# Revit family: ROSENBERG_KHAG-S
name_source: partatom
category: Wyposażenie mechaniczne
revit_build: Autodesk Revit 2017 (Build: 20160225_1515(x64)
units: mm (PartAtom-declared; Revit-internal decimal feet)

## family parameters
Numer OmniClass = 23.75.00.00
Oparty na płaszczyźnie roboczej = Nie
Punkt obliczania pomieszczeń = Nie
Tnij formami wycięć po wczytaniu = Nie
Typ części = Dzieli na
Tytuł OmniClass = Climate Control (HVAC)
Współdzielony = Tak
Wymiar okrągłego złącza = Użyj średnicy
Zawsze pionowo = Tak

## types (12) — shared parameters
2R = 250 mm  [stored 0.82021 ft]
Axis_fan = 40 mm  [stored 0.131234 ft]
Date = 10.2018
Frequency = 50 Hz
Insulation = 20 mm  [stored 0.0656168 ft]
Maintenance_space = Tak
Material = <Wg kategorii>
Opis = Duct Fan
Producent = Rosenberg
Protection Class = IP54
R = 320 mm  [stored 1.04987 ft]
URL = https://www.rosenberg.pl
Version = 1

## per-type parameters (varying)
| type | Air_flow | Current | Fan | Height | Height_connector | Hole | Length | Model | Power | Pressure | Voltage | Weight | Width | Width_connector |
| 500.6FF..WS_400V | 4969.0 m³/h | 3 A | 554 mm | 500 mm  [stored 1.64042 ft] | 500 mm  [stored 1.64042 ft] | 800 mm  [stored 2.62467 ft] | 880 mm | 500.6FF..WS | 1300 W | 741.0 Pa | 400 V | 52.00 kg | 800 mm  [stored 2.62467 ft] | 800 mm  [stored 2.62467 ft] |
| 450.5HF..WS_400V | 3365.0 m³/h | 2 A | 460 mm | 400 mm  [stored 1.31234 ft] | 400 mm  [stored 1.31234 ft] | 170 mm  [stored 0.557743 ft] | 780 mm | 450.5HF..WS | 1300 W | 732.0 Pa | 400 V | 52.00 kg | 700 mm | 700 mm |
| 450.5FA..WS | 2797.0 m³/h | 4 A | 440 mm | 400 mm  [stored 1.31234 ft] | 400 mm  [stored 1.31234 ft] | 170 mm  [stored 0.557743 ft] | 780 mm | 450.5FA..WS | 840 W | 538.0 Pa | 230 V | 64.00 kg | 700 mm | 700 mm |
| 400.5FA..WS_400V | 2645.0 m³/h | 2 A | 395 mm | 350 mm  [stored 1.14829 ft] | 350 mm  [stored 1.14829 ft] | 170 mm  [stored 0.557743 ft] | 700 mm | 400.5FA..WS | 800 W | 564.0 Pa | 400 V | 50.00 kg | 600 mm | 600 mm |
| 400.5FA..WS | 2786.0 m³/h | 4 A | 395 mm | 350 mm  [stored 1.14829 ft] | 350 mm  [stored 1.14829 ft] | 170 mm  [stored 0.557743 ft] | 700 mm | 400.5FA..WS | 800 W | 534.0 Pa | 230 V | 50.00 kg | 600 mm | 600 mm |
| 355.5FA..WS_400V | 2246.0 m³/h | 1 A | 390 mm | 350 mm  [stored 1.14829 ft] | 350 mm  [stored 1.14829 ft] | 170 mm  [stored 0.557743 ft] | 700 mm | 355.5FA..WS | 600 W | 495.0 Pa | 400 V | 50.00 kg | 600 mm | 600 mm |
| 355.4EA..WS | 2074.0 m³/h | 2 A | 390 mm | 350 mm  [stored 1.14829 ft] | 350 mm  [stored 1.14829 ft] | 170 mm  [stored 0.557743 ft] | 700 mm | 355.4EA..WS | 360 W | 314.0 Pa | 230 V | 45.00 kg | 600 mm | 600 mm |
| 280.4EA..WS | 1417.0 m³/h | 2 A | 272 mm | 250 mm  [stored 0.82021 ft] | 250 mm  [stored 0.82021 ft] | 170 mm  [stored 0.557743 ft] | 530 mm  [stored 1.73885 ft] | 280.4EA..WS | 430 W | 523.0 Pa | 230 V | 30.00 kg | 500 mm  [stored 1.64042 ft] | 500 mm  [stored 1.64042 ft] |
| 560.6IF..WS_400V | 7098.0 m³/h | 3 A | 554 mm | 500 mm  [stored 1.64042 ft] | 500 mm  [stored 1.64042 ft] | 800 mm  [stored 2.62467 ft] | 982 mm | 560.6IF..WS | 2600 W | 686.0 Pa | 400 V | 122.00 kg | 1000 mm  [stored 3.28084 ft] | 1000 mm  [stored 3.28084 ft] |
| 315.5FA..WS | 1744.0 m³/h | 4 A | 272 mm | 250 mm  [stored 0.82021 ft] | 250 mm  [stored 0.82021 ft] | 170 mm  [stored 0.557743 ft] | 530 mm  [stored 1.73885 ft] | 315.5FA..WS | 840 W | 786.0 Pa | 230 V | 36.00 kg | 500 mm  [stored 1.64042 ft] | 500 mm  [stored 1.64042 ft] |
| 355.5FA..WS | 2272.0 m³/h | 3 A | 390 mm | 350 mm  [stored 1.14829 ft] | 350 mm  [stored 1.14829 ft] | 170 mm  [stored 0.557743 ft] | 700 mm | 355.5FA..WS | 600 W | 477.0 Pa | 230 V | 50.00 kg | 600 mm | 600 mm |
| 315.4EA..WS | 1094.0 m³/h | 1 A | 272 mm | 250 mm  [stored 0.82021 ft] | 250 mm  [stored 0.82021 ft] | 170 mm  [stored 0.557743 ft] | 530 mm  [stored 1.73885 ft] | 315.4EA..WS | 210 W | 315.0 Pa | 230 V | 32.00 kg | 500 mm  [stored 1.64042 ft] | 500 mm  [stored 1.64042 ft] |

note: [stored X ft] marks values corroborated as IEEE doubles in the binary element streams (Revit-internal decimal feet)

## geometry (parser evidence)
native form markers: Blend x4, Sweep x5
no freeform markers — native parametric forms only
